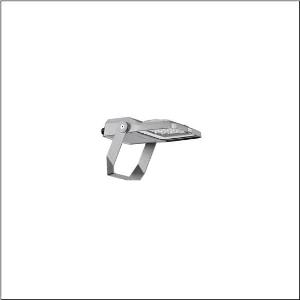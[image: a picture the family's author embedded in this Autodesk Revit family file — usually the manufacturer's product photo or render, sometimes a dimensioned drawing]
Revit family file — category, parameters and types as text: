
# Revit family: floodlight_fl_21_iq_micro___rs12_5xa7761a4b1a_38e5
name_source: partatom
category: Lighting Fixtures
units: mm (PartAtom-declared; Revit-internal decimal feet)

## family parameters
Cut with Voids When Loaded = No
Host = Face
Light Source = No
Part Type = Normal
Room Calculation Point = No
Round Connector Dimension = Use Diameter
Shared = No

## types (1)
- --- (1 x LED, 3220 lm, 23.1 W, 4000K)
    Apparent Load = 23 VA
    CIE Flux Codes = 79 92 99 100 100
    Color Rendering = 70
    Color Temperature = 4000K
    Default Elevation = 1800 mm
    Description = Floodlight FL 21 iQ micro, floodlight, primary light control with lens, of PMMA, primary optical cover: protective disc, of toughened safety glass, transparent, light distribution: RS12, light emission: direct distribution, installation type: surface-mounted, lamps: LED, High Power LED, rated values: 3.220lm | 23,1W | 139,4lm/W (begin service life); end service life: 3.220lm | 23,8W; at 50% lumin. flux: 1.610lm | 11W | 146,4lm/W, colour temperature: 4000K, colour rendering: CRI > 70, light colour: 740, light setting 1 begin service life: 100% | 3.220lm | 23,1W | 139,4lm/W | 4.000K, light setting 1 end service life: 23,8W, further light settings possible, control: optimised constant luminous flux control (CLO 2.0), Desk-Remote (wireless, voltage-free reading and setting of iQ features in the workshop via application-optimized NFC function/RFID function), Light-Fading, Smart-Wire, Night-Set, Lumen-Switch, Temp-Guard, Auto-Match, pre-setting: linear dimming characteristic, with terminal, 6-pole, mains connection: 220..240V, AC, 50/60Hz, luminaire housing, of diecast aluminium, powder-coated, SITECO metallic grey (DB 702S), corrosivity category C5 mid according to DIN EN ISO 12944suitable for swimming poolschlorine-resistant, sealing non-destructively replaceable, mounting bracket, of steel, galvanised, powder-coated, SITECO metallic grey (DB 702S), protection rating (complete): IP66, insulation class (complete): insulation class II (safety insulation), certification: CE, ENEC, VDE, protection symbol: D, impact resistance: IK07, permissible operating ambient temperature: -40..+40°C, permissible operating ambient temperature for outdoor applications: -40..+50°C, standard: DIN EN 12944, LABS conformity tested according to VDMA 24364:2018-05, packaging unit: 1 piece

Light Distribution: RS12
    Height = 65 mm
    Lamp = 1 x LED
    Lamp Light Flux = 3220 lm
    Lamp Power = 23.1 W
    Lamp count = 1
    Length = 312 mm
    Luminous efficacy = 139 lm/W
    Manufacturer = Siteco
    ModVariant = No
    Model = 5XA7761A4B1A
    Mounting Place = Wall
    Mounting Type = Surface mounted
    Number of Poles = 1
    OnlyDefault = Yes
    Power Factor = 1
    Product Name = Floodlight FL 21 iQ micro | RS12
    Product group = floodlight | wall mounted
    ProductGroupID = 2002
    Protection Class = Protection class II
    Protection Degree = IP 66
    RLX_Detail_Level = 1
    RLX_Emergency_Light_Flux = 0 lm
    RLX_Emergency_Type = 0
    RLX_Emergency_Type_DB = No
    RlxData = <blob elided: 75293 chars, md5=eefed25d>
    Socket = socket
    Standby Power = 0 W
    System Light Flux = 3220 lm
    System Power = 23 W
    Type Comments = factory setting: luminous flux: 100 % | dim-lin: 254 | 455 mA
    Type Image = l_1006880.jpg
    URL = http://relux.com
    VarID = @adj_181377
    Voltage = 0 V
    Weight = 0.00 kg
    Width = 230 mm

## geometry (parser evidence)
native form markers: Blend x4, Sweep x12
no freeform markers — native parametric forms only
